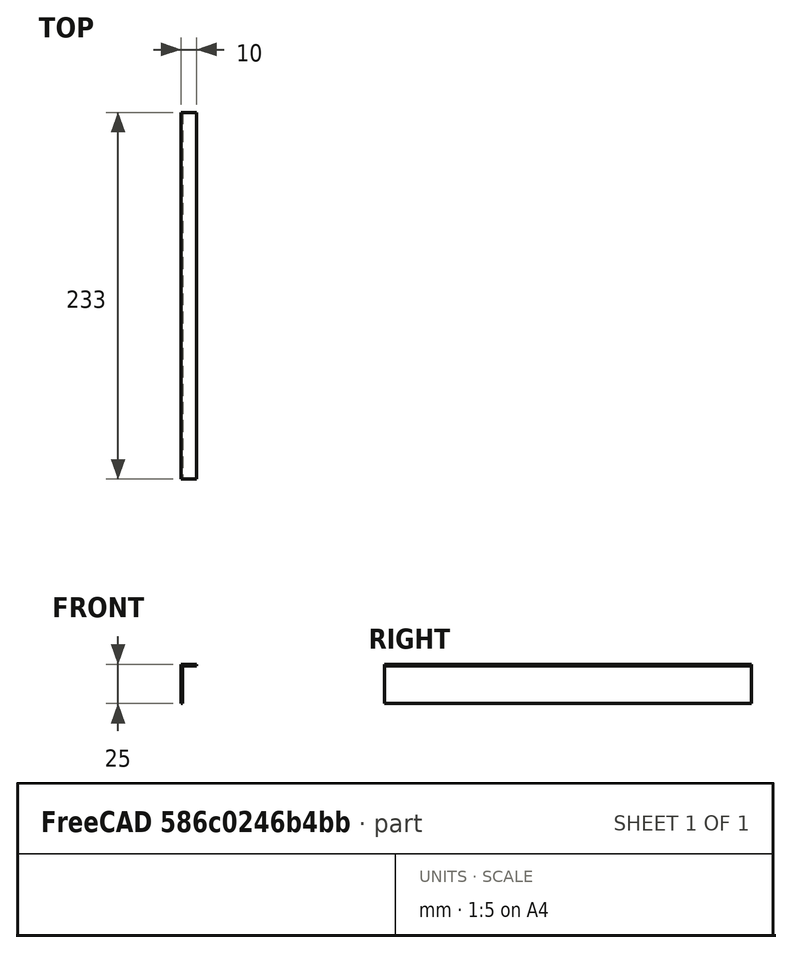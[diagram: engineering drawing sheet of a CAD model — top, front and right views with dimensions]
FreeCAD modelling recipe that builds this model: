
FCSTD DOCUMENT  (FreeCAD 0.21R33694 (Git))
Label: baguette-info-tirettes-la
License: Creative Commons Attribution 3.0
LicenseURL: http://en.wikipedia.org/wiki/Public_domain
objects: Sketcher::SketchObject×1, PartDesign::Pad×1, PartDesign::Body×1
note: 4 computed .brp shape members not serialized (recipe doc carries the construction recipe); baked Part::Feature solids carry a one-line shape summary decoded from their .brp

FEATURE [Sketcher::SketchObject] Sketch
  FullyConstrained = true
  MapMode = 5
  Placement = pos=(0,0,0) rot=(1,0,0;1.5708rad)
  Support = -> [XZ_Plane]
  sketch-geometry (6):
    g0: LineSegment StartX=9 StartY=0 StartZ=0 EndX=0 EndY=0 EndZ=0
    g1: LineSegment StartX=0 StartY=0 StartZ=0 EndX=0 EndY=-24 EndZ=0
    g2: LineSegment StartX=0 StartY=-24 StartZ=0 EndX=-1 EndY=-24 EndZ=0
    g3: LineSegment StartX=-1 StartY=-24 StartZ=0 EndX=-1 EndY=1 EndZ=0
    g4: LineSegment StartX=-1 StartY=1 StartZ=0 EndX=9 EndY=1 EndZ=0
    g5: LineSegment StartX=9 StartY=1 StartZ=0 EndX=9 EndY=0 EndZ=0
  constraints (17):
    c: PointOnObject(g0,g-1)
    c: Coincident(g0,g-1)
    c: Coincident(g0,g1)
    c: PointOnObject(g1,g-2)
    c: Coincident(g1,g2)
    c: Horizontal(g2)
    c: Coincident(g2,g3)
    c: Vertical(g3)
    c: Coincident(g3,g4)
    c: Horizontal(g4)
    c: Coincident(g4,g5)
    c: Coincident(g5,g0)
    c: Vertical(g5)
    c: DistanceY(g5,g5) = 1
    c: DistanceX(g2,g2) = 1
    c: DistanceX(g4,g4) = 10
    c: DistanceY(g3,g3) = 25
FEATURE [PartDesign::Pad] Pad
  Direction = (0,-1,-2e-16)
  Length = 233
  Length2 = 10
  Placement = pos=(0,0,0) rot=(1,0,0;1.5708rad)
  Profile = -> Sketch
  ReferenceAxis = -> Sketch [N_Axis]
  Type = 0
FEATURE [PartDesign::Body] Body
  Group = -> [Sketch,Pad]
  Origin = -> Origin
  Tip = -> Pad
